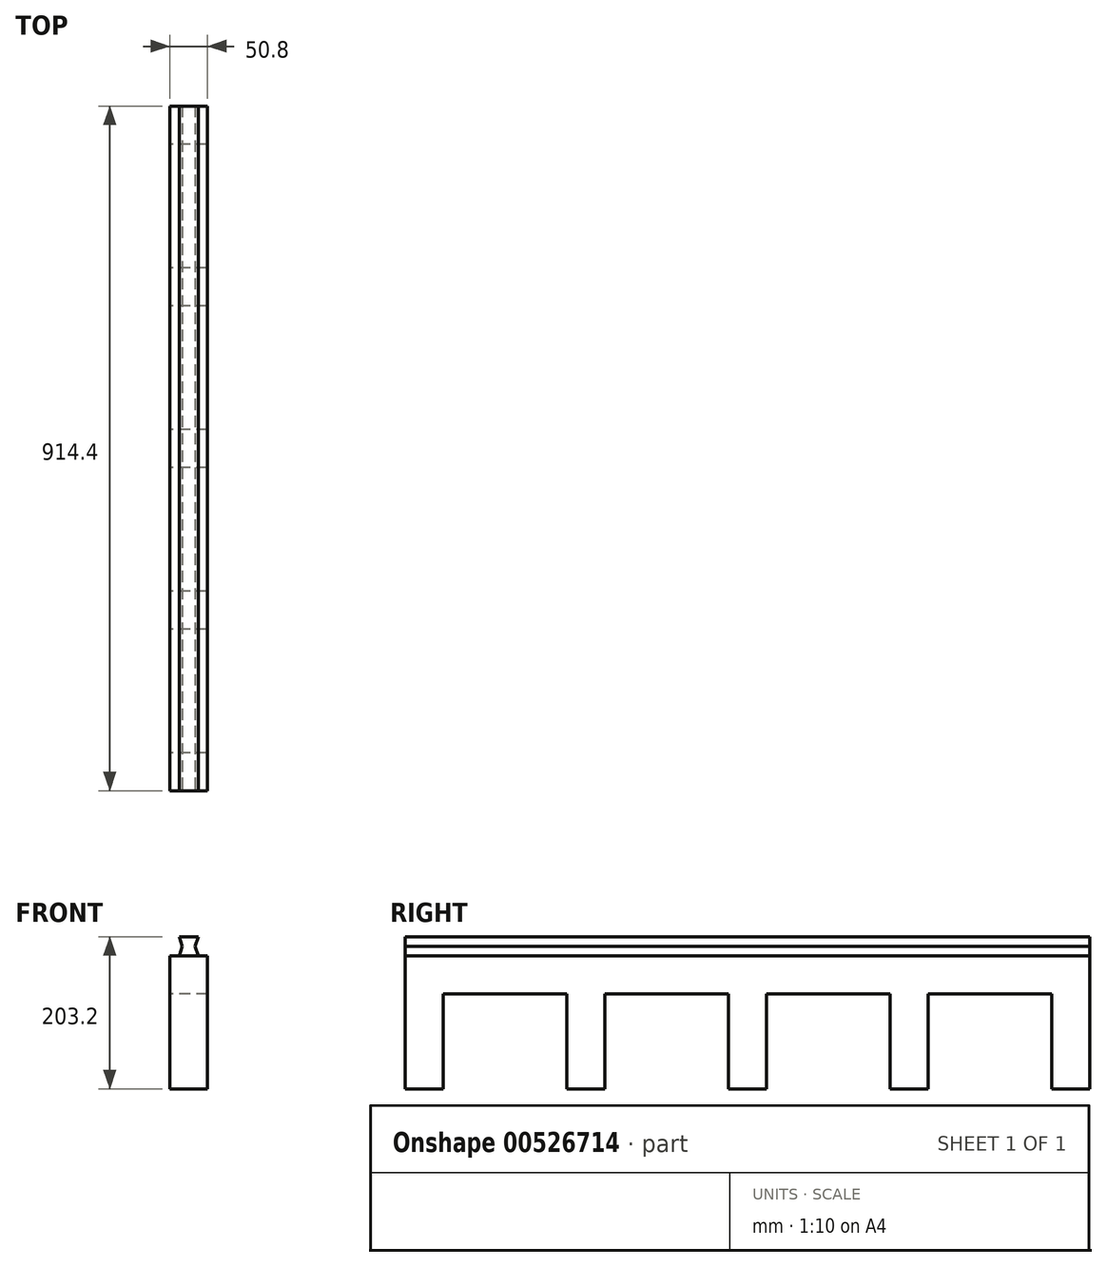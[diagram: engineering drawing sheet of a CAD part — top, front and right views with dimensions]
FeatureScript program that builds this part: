
annotation { "Feature Type Name" : "Feature", "Feature Type Description" : "" }
export const myFeature = defineFeature(function(context is Context, id is Id, definition is map)
    precondition{}
    {
        {
            var Q0;
            Q0=qCreatedBy(makeId("Right.planeOp"),FACE);
            var sketch = newSketch(context, id + "F0", { "sketchPlane" : qUnion([Q0])});
            skLineSegment(sketch, "E0", {"start": v(0, 0) * mm, "end": v(914.4, 0) * mm});
            skLineSegment(sketch, "E1", {"start": v(914.4, 0) * mm, "end": v(914.4, -177.8) * mm});
            skLineSegment(sketch, "E2", {"start": v(914.4, -177.8) * mm, "end": v(863.6, -177.8) * mm});
            skLineSegment(sketch, "E3", {"start": v(863.6, -177.8) * mm, "end": v(863.6, -50.8) * mm});
            skLineSegment(sketch, "E4", {"start": v(863.6, -50.8) * mm, "end": v(698.5, -50.8) * mm});
            skLineSegment(sketch, "E5", {"start": v(698.5, -50.8) * mm, "end": v(698.5, -177.8) * mm});
            skLineSegment(sketch, "E6", {"start": v(698.5, -177.8) * mm, "end": v(647.7, -177.8) * mm});
            skLineSegment(sketch, "E7", {"start": v(647.7, -177.8) * mm, "end": v(647.7, -50.8) * mm});
            skLineSegment(sketch, "E8", {"start": v(647.7, -50.8) * mm, "end": v(482.6, -50.8) * mm});
            skLineSegment(sketch, "E9", {"start": v(482.6, -50.8) * mm, "end": v(482.6, -177.8) * mm});
            skPoint(sketch, "E9.endSnap0", {"position": v(673.1, -177.8) * mm});
            skLineSegment(sketch, "E10", {"start": v(482.6, -177.8) * mm, "end": v(431.8, -177.8) * mm});
            skLineSegment(sketch, "E11", {"start": v(431.8, -177.8) * mm, "end": v(431.8, -50.8) * mm});
            skLineSegment(sketch, "E12", {"start": v(431.8, -50.8) * mm, "end": v(266.7, -50.8) * mm});
            skLineSegment(sketch, "E13", {"start": v(266.7, -50.8) * mm, "end": v(266.7, -177.8) * mm});
            skLineSegment(sketch, "E14", {"start": v(266.7, -177.8) * mm, "end": v(215.9, -177.8) * mm});
            skLineSegment(sketch, "E15", {"start": v(215.9, -177.8) * mm, "end": v(215.9, -50.8) * mm});
            skLineSegment(sketch, "E16", {"start": v(215.9, -50.8) * mm, "end": v(50.8, -50.8) * mm});
            skLineSegment(sketch, "E17", {"start": v(50.8, -50.8) * mm, "end": v(50.8, -177.8) * mm});
            skLineSegment(sketch, "E18", {"start": v(50.8, -177.8) * mm, "end": v(0, -177.8) * mm});
            skLineSegment(sketch, "E19", {"start": v(0, -177.8) * mm, "end": v(0, 0) * mm});
            skSolve(sketch);
        }
        {
            var Q0;
            Q0=makeQuery(id+"F0.imprint","IMPRINT",FACE,{"disambiguationData":[TD([[makeQuery(id+"F0.imprint","IMPRINT",EDGE,{"derivedFrom":sQuery(id+"F0.wireOp",EDGE,"E0")}),-1.0]])]});
            extrude(context, id + "F1", {"entities" : qUnion([Q0]), "depth" : 50.8 * mm, "offsetDistance" : 25.4 * mm});
        }
        {
            var Q0;
            Q0=qCreatedBy(makeId("Front.planeOp"),FACE);
            var sketch = newSketch(context, id + "F2", { "sketchPlane" : qUnion([Q0])});
            skLineSegment(sketch, "E20", {"start": v(0, 0) * mm, "end": v(12.7, 0) * mm});
            skLineSegment(sketch, "E21.bottom", {"start": v(12.7, 0) * mm, "end": v(38.1, 0) * mm});
            skLineSegment(sketch, "E22", {"start": v(12.7, 25.4) * mm, "end": v(38.1, 25.4) * mm});
            skLineSegment(sketch, "E23", {"start": v(12.7, 0) * mm, "end": v(16.63, 12.7) * mm});
            skLineSegment(sketch, "E24", {"start": v(16.63, 12.7) * mm, "end": v(12.7, 25.4) * mm});
            skLineSegment(sketch, "E25", {"start": v(25.4, 25.4) * mm, "end": v(25.4, 0) * mm, "construction": true});
            skLineSegment(sketch, "E26.MirrorCS", {"start": v(34.17, 12.7) * mm, "end": v(38.1, 25.4) * mm});
            skLineSegment(sketch, "E27.MirrorCS", {"start": v(38.1, 0) * mm, "end": v(34.17, 12.7) * mm});
            skSolve(sketch);
        }
        {
            var Q0;
            Q0=makeQuery(id+"F2.imprint","IMPRINT",FACE,{"disambiguationData":[TD([[makeQuery(id+"F2.imprint","IMPRINT",EDGE,{"derivedFrom":sQuery(id+"F2.wireOp",EDGE,"E21.bottom")}),1.0]])]});
            extrude(context, id + "F3", {"entities" : qUnion([Q0]), "oppositeDirection" : true, "depth" : 914.4 * mm, "offsetDistance" : 25.4 * mm});
        }
    });
